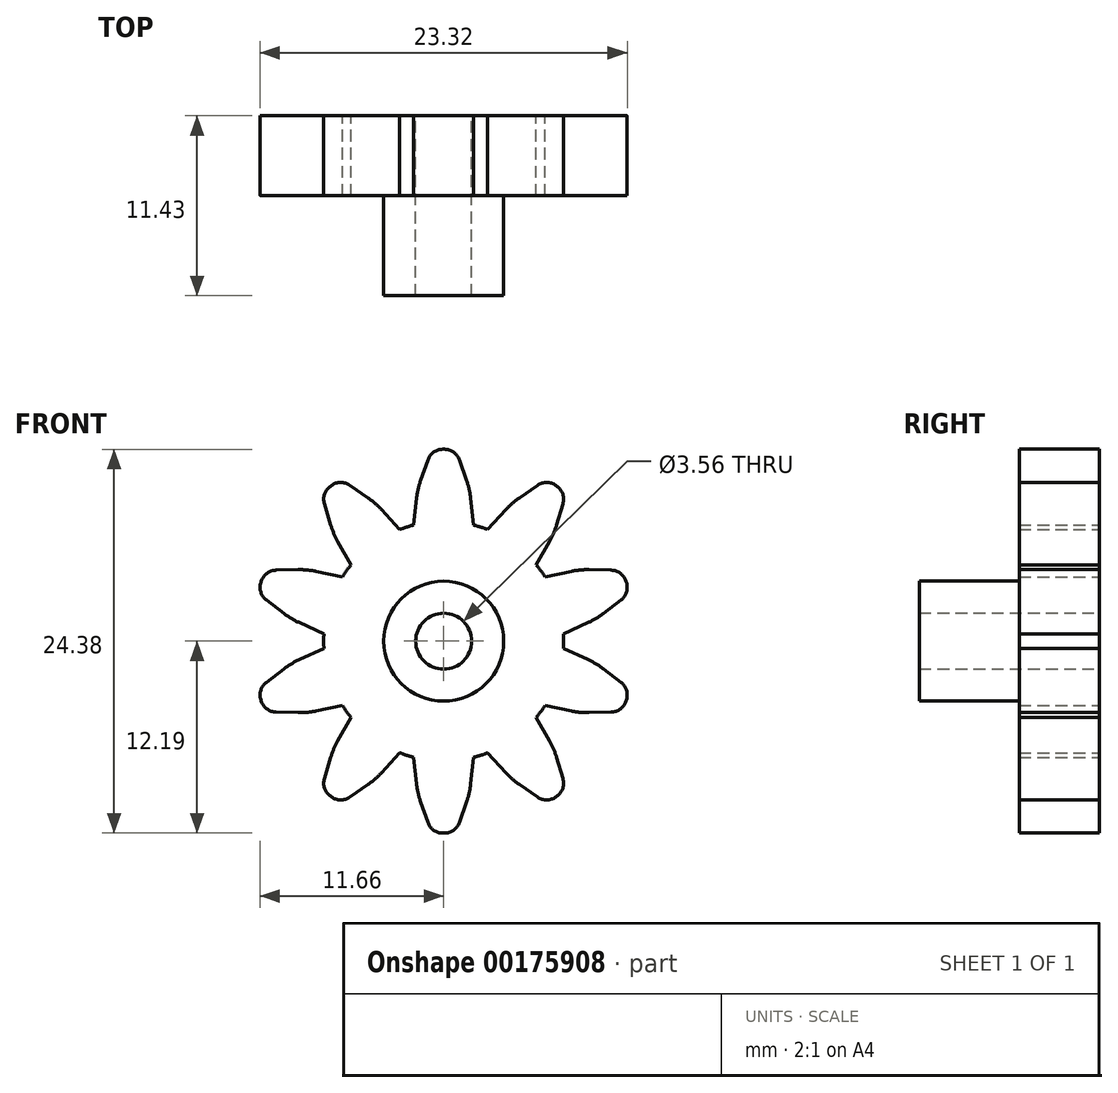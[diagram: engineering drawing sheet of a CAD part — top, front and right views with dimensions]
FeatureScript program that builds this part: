
annotation { "Feature Type Name" : "Feature", "Feature Type Description" : "" }
export const myFeature = defineFeature(function(context is Context, id is Id, definition is map)
    precondition{}
    {
        {
            var Q0;
            Q0=qCreatedBy(makeId("Front.planeOp"),FACE);
            var sketch = newSketch(context, id + "F0", { "sketchPlane" : qUnion([Q0])});
            skCircle(sketch, "E0", {"center": v(0, 0) * mm, "radius": 7.62 * mm});
            skLineSegment(sketch, "E1", {"start": v(-1.9, 7.38) * mm, "end": v(-0.76, 12.2) * mm, "construction": true});
            skLineSegment(sketch, "E2", {"start": v(-0.76, 12.2) * mm, "end": v(0.76, 12.2) * mm});
            skLineSegment(sketch, "E3", {"start": v(0.76, 12.2) * mm, "end": v(1.9, 7.38) * mm, "construction": true});
            skLineSegment(sketch, "E4", {"start": v(-1.9, 7.38) * mm, "end": v(-1.65, 9.65) * mm});
            skPoint(sketch, "E4.endSnap0", {"position": v(-1.33, 9.79) * mm});
            skLineSegment(sketch, "E5", {"start": v(-1.65, 9.65) * mm, "end": v(-0.76, 12.2) * mm});
            skLineSegment(sketch, "E6", {"start": v(1.9, 7.38) * mm, "end": v(1.65, 9.65) * mm});
            skPoint(sketch, "E6.endSnap0", {"position": v(1.33, 9.79) * mm});
            skLineSegment(sketch, "E7", {"start": v(1.65, 9.65) * mm, "end": v(0.76, 12.2) * mm});
            skLineSegment(sketch, "E8.1.0", {"start": v(-7.78, 9.42) * mm, "end": v(-6.55, 10.31) * mm});
            skLineSegment(sketch, "E8.1.1", {"start": v(-4.34, 8.78) * mm, "end": v(-6.55, 10.31) * mm});
            skLineSegment(sketch, "E8.1.2", {"start": v(-2.8, 7.09) * mm, "end": v(-4.34, 8.78) * mm});
            skLineSegment(sketch, "E8.1.3", {"start": v(-7, 6.84) * mm, "end": v(-7.78, 9.42) * mm});
            skLineSegment(sketch, "E8.1.4", {"start": v(-5.88, 4.85) * mm, "end": v(-7, 6.84) * mm});
            skLineSegment(sketch, "E8.2.0", {"start": v(-11.83, 3.04) * mm, "end": v(-11.36, 4.5) * mm});
            skLineSegment(sketch, "E8.2.1", {"start": v(-8.67, 4.55) * mm, "end": v(-11.36, 4.5) * mm});
            skLineSegment(sketch, "E8.2.2", {"start": v(-6.43, 4.1) * mm, "end": v(-8.67, 4.55) * mm});
            skLineSegment(sketch, "E8.2.3", {"start": v(-9.69, 1.41) * mm, "end": v(-11.83, 3.04) * mm});
            skLineSegment(sketch, "E8.2.4", {"start": v(-7.6, 0.47) * mm, "end": v(-9.69, 1.41) * mm});
            skLineSegment(sketch, "E8.3.0", {"start": v(-11.36, -4.5) * mm, "end": v(-11.83, -3.04) * mm});
            skLineSegment(sketch, "E8.3.1", {"start": v(-9.69, -1.41) * mm, "end": v(-11.83, -3.04) * mm});
            skLineSegment(sketch, "E8.3.2", {"start": v(-7.6, -0.47) * mm, "end": v(-9.69, -1.41) * mm});
            skLineSegment(sketch, "E8.3.3", {"start": v(-8.67, -4.55) * mm, "end": v(-11.36, -4.5) * mm});
            skLineSegment(sketch, "E8.3.4", {"start": v(-6.43, -4.1) * mm, "end": v(-8.67, -4.55) * mm});
            skLineSegment(sketch, "E8.4.0", {"start": v(-6.55, -10.31) * mm, "end": v(-7.78, -9.42) * mm});
            skLineSegment(sketch, "E8.4.1", {"start": v(-7, -6.84) * mm, "end": v(-7.78, -9.42) * mm});
            skLineSegment(sketch, "E8.4.2", {"start": v(-5.88, -4.85) * mm, "end": v(-7, -6.84) * mm});
            skLineSegment(sketch, "E8.4.3", {"start": v(-4.34, -8.78) * mm, "end": v(-6.55, -10.31) * mm});
            skLineSegment(sketch, "E8.4.4", {"start": v(-2.8, -7.09) * mm, "end": v(-4.34, -8.78) * mm});
            skLineSegment(sketch, "E8.5.0", {"start": v(0.76, -12.2) * mm, "end": v(-0.76, -12.2) * mm});
            skLineSegment(sketch, "E8.5.1", {"start": v(-1.65, -9.65) * mm, "end": v(-0.76, -12.2) * mm});
            skLineSegment(sketch, "E8.5.2", {"start": v(-1.9, -7.38) * mm, "end": v(-1.65, -9.65) * mm});
            skLineSegment(sketch, "E8.5.3", {"start": v(1.65, -9.65) * mm, "end": v(0.76, -12.2) * mm});
            skLineSegment(sketch, "E8.5.4", {"start": v(1.9, -7.38) * mm, "end": v(1.65, -9.65) * mm});
            skLineSegment(sketch, "E8.6.0", {"start": v(7.78, -9.42) * mm, "end": v(6.55, -10.31) * mm});
            skLineSegment(sketch, "E8.6.1", {"start": v(4.34, -8.78) * mm, "end": v(6.55, -10.31) * mm});
            skLineSegment(sketch, "E8.6.2", {"start": v(2.8, -7.09) * mm, "end": v(4.34, -8.78) * mm});
            skLineSegment(sketch, "E8.6.3", {"start": v(7, -6.84) * mm, "end": v(7.78, -9.42) * mm});
            skLineSegment(sketch, "E8.6.4", {"start": v(5.88, -4.85) * mm, "end": v(7, -6.84) * mm});
            skLineSegment(sketch, "E8.7.0", {"start": v(11.83, -3.04) * mm, "end": v(11.36, -4.5) * mm});
            skLineSegment(sketch, "E8.7.1", {"start": v(8.67, -4.55) * mm, "end": v(11.36, -4.5) * mm});
            skLineSegment(sketch, "E8.7.2", {"start": v(6.43, -4.1) * mm, "end": v(8.67, -4.55) * mm});
            skLineSegment(sketch, "E8.7.3", {"start": v(9.69, -1.41) * mm, "end": v(11.83, -3.04) * mm});
            skLineSegment(sketch, "E8.7.4", {"start": v(7.6, -0.47) * mm, "end": v(9.69, -1.41) * mm});
            skLineSegment(sketch, "E8.8.0", {"start": v(11.36, 4.5) * mm, "end": v(11.83, 3.04) * mm});
            skLineSegment(sketch, "E8.8.1", {"start": v(9.69, 1.41) * mm, "end": v(11.83, 3.04) * mm});
            skLineSegment(sketch, "E8.8.2", {"start": v(7.6, 0.47) * mm, "end": v(9.69, 1.41) * mm});
            skLineSegment(sketch, "E8.8.3", {"start": v(8.67, 4.55) * mm, "end": v(11.36, 4.5) * mm});
            skLineSegment(sketch, "E8.8.4", {"start": v(6.43, 4.1) * mm, "end": v(8.67, 4.55) * mm});
            skLineSegment(sketch, "E8.9.0", {"start": v(6.55, 10.31) * mm, "end": v(7.78, 9.42) * mm});
            skLineSegment(sketch, "E8.9.1", {"start": v(7, 6.84) * mm, "end": v(7.78, 9.42) * mm});
            skLineSegment(sketch, "E8.9.2", {"start": v(5.88, 4.85) * mm, "end": v(7, 6.84) * mm});
            skLineSegment(sketch, "E8.9.3", {"start": v(4.34, 8.78) * mm, "end": v(6.55, 10.31) * mm});
            skLineSegment(sketch, "E8.9.4", {"start": v(2.8, 7.09) * mm, "end": v(4.34, 8.78) * mm});
            skCircle(sketch, "E9", {"center": v(0, 0) * mm, "radius": 1.78 * mm});
            skSolve(sketch);
        }
        {
            var Q0;
            Q0 = qSketchRegion(id + "F0", true);
            extrude(context, id + "F1", {"entities" : qUnion([Q0]), "depth" : 5.08 * mm});
        }
        {
            var Q0;
            Q0=makeQuery(id+"F1.opExtrude","CAP_FACE",FACE,{"disambiguationData":[OSD([sQuery(id+"F0.wireOp",EDGE,"E0"),sQuery(id+"F0.wireOp",EDGE,"E2"),sQuery(id+"F0.wireOp",EDGE,"E4"),sQuery(id+"F0.wireOp",EDGE,"E5"),sQuery(id+"F0.wireOp",EDGE,"E6"),sQuery(id+"F0.wireOp",EDGE,"E7"),sQuery(id+"F0.wireOp",EDGE,"E8.1.0"),sQuery(id+"F0.wireOp",EDGE,"E8.1.1"),sQuery(id+"F0.wireOp",EDGE,"E8.1.2"),sQuery(id+"F0.wireOp",EDGE,"E8.1.3"),sQuery(id+"F0.wireOp",EDGE,"E8.1.4"),sQuery(id+"F0.wireOp",EDGE,"E8.2.0"),sQuery(id+"F0.wireOp",EDGE,"E8.2.1"),sQuery(id+"F0.wireOp",EDGE,"E8.2.2"),sQuery(id+"F0.wireOp",EDGE,"E8.2.3"),sQuery(id+"F0.wireOp",EDGE,"E8.2.4"),sQuery(id+"F0.wireOp",EDGE,"E8.3.0"),sQuery(id+"F0.wireOp",EDGE,"E8.3.1"),sQuery(id+"F0.wireOp",EDGE,"E8.3.2"),sQuery(id+"F0.wireOp",EDGE,"E8.3.3"),sQuery(id+"F0.wireOp",EDGE,"E8.3.4"),sQuery(id+"F0.wireOp",EDGE,"E8.4.0"),sQuery(id+"F0.wireOp",EDGE,"E8.4.1"),sQuery(id+"F0.wireOp",EDGE,"E8.4.2"),sQuery(id+"F0.wireOp",EDGE,"E8.4.3"),sQuery(id+"F0.wireOp",EDGE,"E8.4.4"),sQuery(id+"F0.wireOp",EDGE,"E8.5.0"),sQuery(id+"F0.wireOp",EDGE,"E8.5.1"),sQuery(id+"F0.wireOp",EDGE,"E8.5.2"),sQuery(id+"F0.wireOp",EDGE,"E8.5.3"),sQuery(id+"F0.wireOp",EDGE,"E8.5.4"),sQuery(id+"F0.wireOp",EDGE,"E8.6.0"),sQuery(id+"F0.wireOp",EDGE,"E8.6.1"),sQuery(id+"F0.wireOp",EDGE,"E8.6.2"),sQuery(id+"F0.wireOp",EDGE,"E8.6.3"),sQuery(id+"F0.wireOp",EDGE,"E8.6.4"),sQuery(id+"F0.wireOp",EDGE,"E8.7.0"),sQuery(id+"F0.wireOp",EDGE,"E8.7.1"),sQuery(id+"F0.wireOp",EDGE,"E8.7.2"),sQuery(id+"F0.wireOp",EDGE,"E8.7.3"),sQuery(id+"F0.wireOp",EDGE,"E8.7.4"),sQuery(id+"F0.wireOp",EDGE,"E8.8.0"),sQuery(id+"F0.wireOp",EDGE,"E8.8.1"),sQuery(id+"F0.wireOp",EDGE,"E8.8.2"),sQuery(id+"F0.wireOp",EDGE,"E8.8.3"),sQuery(id+"F0.wireOp",EDGE,"E8.8.4"),sQuery(id+"F0.wireOp",EDGE,"E8.9.0"),sQuery(id+"F0.wireOp",EDGE,"E8.9.1"),sQuery(id+"F0.wireOp",EDGE,"E8.9.2"),sQuery(id+"F0.wireOp",EDGE,"E8.9.3"),sQuery(id+"F0.wireOp",EDGE,"E8.9.4"),sQuery(id+"F0.wireOp",EDGE,"E9")])],"isStart":false});
            var sketch = newSketch(context, id + "F2", { "sketchPlane" : qUnion([Q0])});
            skCircle(sketch, "E10.0", {"center": v(0, 0) * mm, "radius": 1.78 * mm});
            skCircle(sketch, "E11", {"center": v(0, 0) * mm, "radius": 3.81 * mm});
            skSolve(sketch);
        }
        {
            var Q0;
            Q0 = qSketchRegion(id + "F2", true);
            extrude(context, id + "F3", {"entities" : qUnion([Q0]), "operationType" : NewBodyOperationType.ADD, "depth" : 6.35 * mm});
        }
        {
            var Q0;
            Q0=makeQuery(id+"F1.opExtrude","SWEPT_EDGE",EDGE,{"disambiguationData":[OSD([sQuery(id+"F0.wireOp",EDGE,"E8.9.1"),sQuery(id+"F0.wireOp",EDGE,"E8.9.2")])]});
            var Q1;
            Q1=makeQuery(id+"F1.opExtrude","SWEPT_EDGE",EDGE,{"disambiguationData":[OSD([sQuery(id+"F0.wireOp",EDGE,"E8.9.3"),sQuery(id+"F0.wireOp",EDGE,"E8.9.4")])]});
            var Q2;
            Q2=makeQuery(id+"F1.opExtrude","SWEPT_EDGE",EDGE,{"disambiguationData":[OSD([sQuery(id+"F0.wireOp",EDGE,"E6"),sQuery(id+"F0.wireOp",EDGE,"E7")])]});
            var Q3;
            Q3=makeQuery(id+"F1.opExtrude","SWEPT_EDGE",EDGE,{"disambiguationData":[OSD([sQuery(id+"F0.wireOp",EDGE,"E8.1.1"),sQuery(id+"F0.wireOp",EDGE,"E8.1.2")])]});
            var Q4;
            Q4=makeQuery(id+"F1.opExtrude","SWEPT_EDGE",EDGE,{"disambiguationData":[OSD([sQuery(id+"F0.wireOp",EDGE,"E8.2.1"),sQuery(id+"F0.wireOp",EDGE,"E8.2.2")])]});
            var Q5;
            Q5=makeQuery(id+"F1.opExtrude","SWEPT_EDGE",EDGE,{"disambiguationData":[OSD([sQuery(id+"F0.wireOp",EDGE,"E8.3.1"),sQuery(id+"F0.wireOp",EDGE,"E8.3.2")])]});
            var Q6;
            Q6=makeQuery(id+"F1.opExtrude","SWEPT_EDGE",EDGE,{"disambiguationData":[OSD([sQuery(id+"F0.wireOp",EDGE,"E8.4.1"),sQuery(id+"F0.wireOp",EDGE,"E8.4.2")])]});
            var Q7;
            Q7=makeQuery(id+"F1.opExtrude","SWEPT_EDGE",EDGE,{"disambiguationData":[OSD([sQuery(id+"F0.wireOp",EDGE,"E8.5.1"),sQuery(id+"F0.wireOp",EDGE,"E8.5.2")])]});
            var Q8;
            Q8=makeQuery(id+"F1.opExtrude","SWEPT_EDGE",EDGE,{"disambiguationData":[OSD([sQuery(id+"F0.wireOp",EDGE,"E8.6.1"),sQuery(id+"F0.wireOp",EDGE,"E8.6.2")])]});
            var Q9;
            Q9=makeQuery(id+"F1.opExtrude","SWEPT_EDGE",EDGE,{"disambiguationData":[OSD([sQuery(id+"F0.wireOp",EDGE,"E8.7.1"),sQuery(id+"F0.wireOp",EDGE,"E8.7.2")])]});
            var Q10;
            Q10=makeQuery(id+"F1.opExtrude","SWEPT_EDGE",EDGE,{"disambiguationData":[OSD([sQuery(id+"F0.wireOp",EDGE,"E8.8.1"),sQuery(id+"F0.wireOp",EDGE,"E8.8.2")])]});
            var Q11;
            Q11=makeQuery(id+"F1.opExtrude","SWEPT_EDGE",EDGE,{"disambiguationData":[OSD([sQuery(id+"F0.wireOp",EDGE,"E8.7.3"),sQuery(id+"F0.wireOp",EDGE,"E8.7.4")])]});
            var Q12;
            Q12=makeQuery(id+"F1.opExtrude","SWEPT_EDGE",EDGE,{"disambiguationData":[OSD([sQuery(id+"F0.wireOp",EDGE,"E8.8.3"),sQuery(id+"F0.wireOp",EDGE,"E8.8.4")])]});
            var Q13;
            Q13=makeQuery(id+"F1.opExtrude","SWEPT_EDGE",EDGE,{"disambiguationData":[OSD([sQuery(id+"F0.wireOp",EDGE,"E4"),sQuery(id+"F0.wireOp",EDGE,"E5")])]});
            var Q14;
            Q14=makeQuery(id+"F1.opExtrude","SWEPT_EDGE",EDGE,{"disambiguationData":[OSD([sQuery(id+"F0.wireOp",EDGE,"E8.1.3"),sQuery(id+"F0.wireOp",EDGE,"E8.1.4")])]});
            var Q15;
            Q15=makeQuery(id+"F1.opExtrude","SWEPT_EDGE",EDGE,{"disambiguationData":[OSD([sQuery(id+"F0.wireOp",EDGE,"E8.2.3"),sQuery(id+"F0.wireOp",EDGE,"E8.2.4")])]});
            var Q16;
            Q16=makeQuery(id+"F1.opExtrude","SWEPT_EDGE",EDGE,{"disambiguationData":[OSD([sQuery(id+"F0.wireOp",EDGE,"E8.3.3"),sQuery(id+"F0.wireOp",EDGE,"E8.3.4")])]});
            var Q17;
            Q17=makeQuery(id+"F1.opExtrude","SWEPT_EDGE",EDGE,{"disambiguationData":[OSD([sQuery(id+"F0.wireOp",EDGE,"E8.4.3"),sQuery(id+"F0.wireOp",EDGE,"E8.4.4")])]});
            var Q18;
            Q18=makeQuery(id+"F1.opExtrude","SWEPT_EDGE",EDGE,{"disambiguationData":[OSD([sQuery(id+"F0.wireOp",EDGE,"E8.5.3"),sQuery(id+"F0.wireOp",EDGE,"E8.5.4")])]});
            var Q19;
            Q19=makeQuery(id+"F1.opExtrude","SWEPT_EDGE",EDGE,{"disambiguationData":[OSD([sQuery(id+"F0.wireOp",EDGE,"E8.6.3"),sQuery(id+"F0.wireOp",EDGE,"E8.6.4")])]});
            fillet(context, id + "F4", {"entities" : qUnion([Q0, Q1, Q2, Q3, Q4, Q5, Q6, Q7, Q8, Q9, Q10, Q11, Q12, Q13, Q14, Q15, Q16, Q17, Q18, Q19]), "radius" : 5.08 * mm, "tangentPropagation" : true, "allowEdgeOverflow" : false});
        }
        {
            var Q0;
            Q0=makeQuery(id+"F1.opExtrude","SWEPT_EDGE",EDGE,{"disambiguationData":[OSD([sQuery(id+"F0.wireOp",EDGE,"E2"),sQuery(id+"F0.wireOp",EDGE,"E7")])]});
            var Q1;
            Q1=makeQuery(id+"F1.opExtrude","SWEPT_EDGE",EDGE,{"disambiguationData":[OSD([sQuery(id+"F0.wireOp",EDGE,"E2"),sQuery(id+"F0.wireOp",EDGE,"E5")])]});
            var Q2;
            Q2=makeQuery(id+"F1.opExtrude","SWEPT_EDGE",EDGE,{"disambiguationData":[OSD([sQuery(id+"F0.wireOp",EDGE,"E8.1.0"),sQuery(id+"F0.wireOp",EDGE,"E8.1.1")])]});
            var Q3;
            Q3=makeQuery(id+"F1.opExtrude","SWEPT_EDGE",EDGE,{"disambiguationData":[OSD([sQuery(id+"F0.wireOp",EDGE,"E8.1.0"),sQuery(id+"F0.wireOp",EDGE,"E8.1.3")])]});
            var Q4;
            Q4=makeQuery(id+"F1.opExtrude","SWEPT_EDGE",EDGE,{"disambiguationData":[OSD([sQuery(id+"F0.wireOp",EDGE,"E8.2.0"),sQuery(id+"F0.wireOp",EDGE,"E8.2.1")])]});
            var Q5;
            Q5=makeQuery(id+"F1.opExtrude","SWEPT_EDGE",EDGE,{"disambiguationData":[OSD([sQuery(id+"F0.wireOp",EDGE,"E8.9.0"),sQuery(id+"F0.wireOp",EDGE,"E8.9.3")])]});
            var Q6;
            Q6=makeQuery(id+"F1.opExtrude","SWEPT_EDGE",EDGE,{"disambiguationData":[OSD([sQuery(id+"F0.wireOp",EDGE,"E8.9.0"),sQuery(id+"F0.wireOp",EDGE,"E8.9.1")])]});
            var Q7;
            Q7=makeQuery(id+"F1.opExtrude","SWEPT_EDGE",EDGE,{"disambiguationData":[OSD([sQuery(id+"F0.wireOp",EDGE,"E8.8.0"),sQuery(id+"F0.wireOp",EDGE,"E8.8.3")])]});
            var Q8;
            Q8=makeQuery(id+"F1.opExtrude","SWEPT_EDGE",EDGE,{"disambiguationData":[OSD([sQuery(id+"F0.wireOp",EDGE,"E8.2.0"),sQuery(id+"F0.wireOp",EDGE,"E8.2.3")])]});
            var Q9;
            Q9=makeQuery(id+"F1.opExtrude","SWEPT_EDGE",EDGE,{"disambiguationData":[OSD([sQuery(id+"F0.wireOp",EDGE,"E8.3.0"),sQuery(id+"F0.wireOp",EDGE,"E8.3.1")])]});
            var Q10;
            Q10=makeQuery(id+"F1.opExtrude","SWEPT_EDGE",EDGE,{"disambiguationData":[OSD([sQuery(id+"F0.wireOp",EDGE,"E8.3.0"),sQuery(id+"F0.wireOp",EDGE,"E8.3.3")])]});
            var Q11;
            Q11=makeQuery(id+"F1.opExtrude","SWEPT_EDGE",EDGE,{"disambiguationData":[OSD([sQuery(id+"F0.wireOp",EDGE,"E8.4.0"),sQuery(id+"F0.wireOp",EDGE,"E8.4.1")])]});
            var Q12;
            Q12=makeQuery(id+"F1.opExtrude","SWEPT_EDGE",EDGE,{"disambiguationData":[OSD([sQuery(id+"F0.wireOp",EDGE,"E8.4.0"),sQuery(id+"F0.wireOp",EDGE,"E8.4.3")])]});
            var Q13;
            Q13=makeQuery(id+"F1.opExtrude","SWEPT_EDGE",EDGE,{"disambiguationData":[OSD([sQuery(id+"F0.wireOp",EDGE,"E8.5.0"),sQuery(id+"F0.wireOp",EDGE,"E8.5.1")])]});
            var Q14;
            Q14=makeQuery(id+"F1.opExtrude","SWEPT_EDGE",EDGE,{"disambiguationData":[OSD([sQuery(id+"F0.wireOp",EDGE,"E8.5.0"),sQuery(id+"F0.wireOp",EDGE,"E8.5.3")])]});
            var Q15;
            Q15=makeQuery(id+"F1.opExtrude","SWEPT_EDGE",EDGE,{"disambiguationData":[OSD([sQuery(id+"F0.wireOp",EDGE,"E8.6.0"),sQuery(id+"F0.wireOp",EDGE,"E8.6.1")])]});
            var Q16;
            Q16=makeQuery(id+"F1.opExtrude","SWEPT_EDGE",EDGE,{"disambiguationData":[OSD([sQuery(id+"F0.wireOp",EDGE,"E8.6.0"),sQuery(id+"F0.wireOp",EDGE,"E8.6.3")])]});
            var Q17;
            Q17=makeQuery(id+"F1.opExtrude","SWEPT_EDGE",EDGE,{"disambiguationData":[OSD([sQuery(id+"F0.wireOp",EDGE,"E8.7.0"),sQuery(id+"F0.wireOp",EDGE,"E8.7.3")])]});
            var Q18;
            Q18=makeQuery(id+"F1.opExtrude","SWEPT_EDGE",EDGE,{"disambiguationData":[OSD([sQuery(id+"F0.wireOp",EDGE,"E8.7.0"),sQuery(id+"F0.wireOp",EDGE,"E8.7.1")])]});
            var Q19;
            Q19=makeQuery(id+"F1.opExtrude","SWEPT_EDGE",EDGE,{"disambiguationData":[OSD([sQuery(id+"F0.wireOp",EDGE,"E8.8.0"),sQuery(id+"F0.wireOp",EDGE,"E8.8.1")])]});
            fillet(context, id + "F5", {"entities" : qUnion([Q0, Q1, Q2, Q3, Q4, Q5, Q6, Q7, Q8, Q9, Q10, Q11, Q12, Q13, Q14, Q15, Q16, Q17, Q18, Q19]), "radius" : 1.02 * mm, "tangentPropagation" : true, "allowEdgeOverflow" : false});
        }
    });
